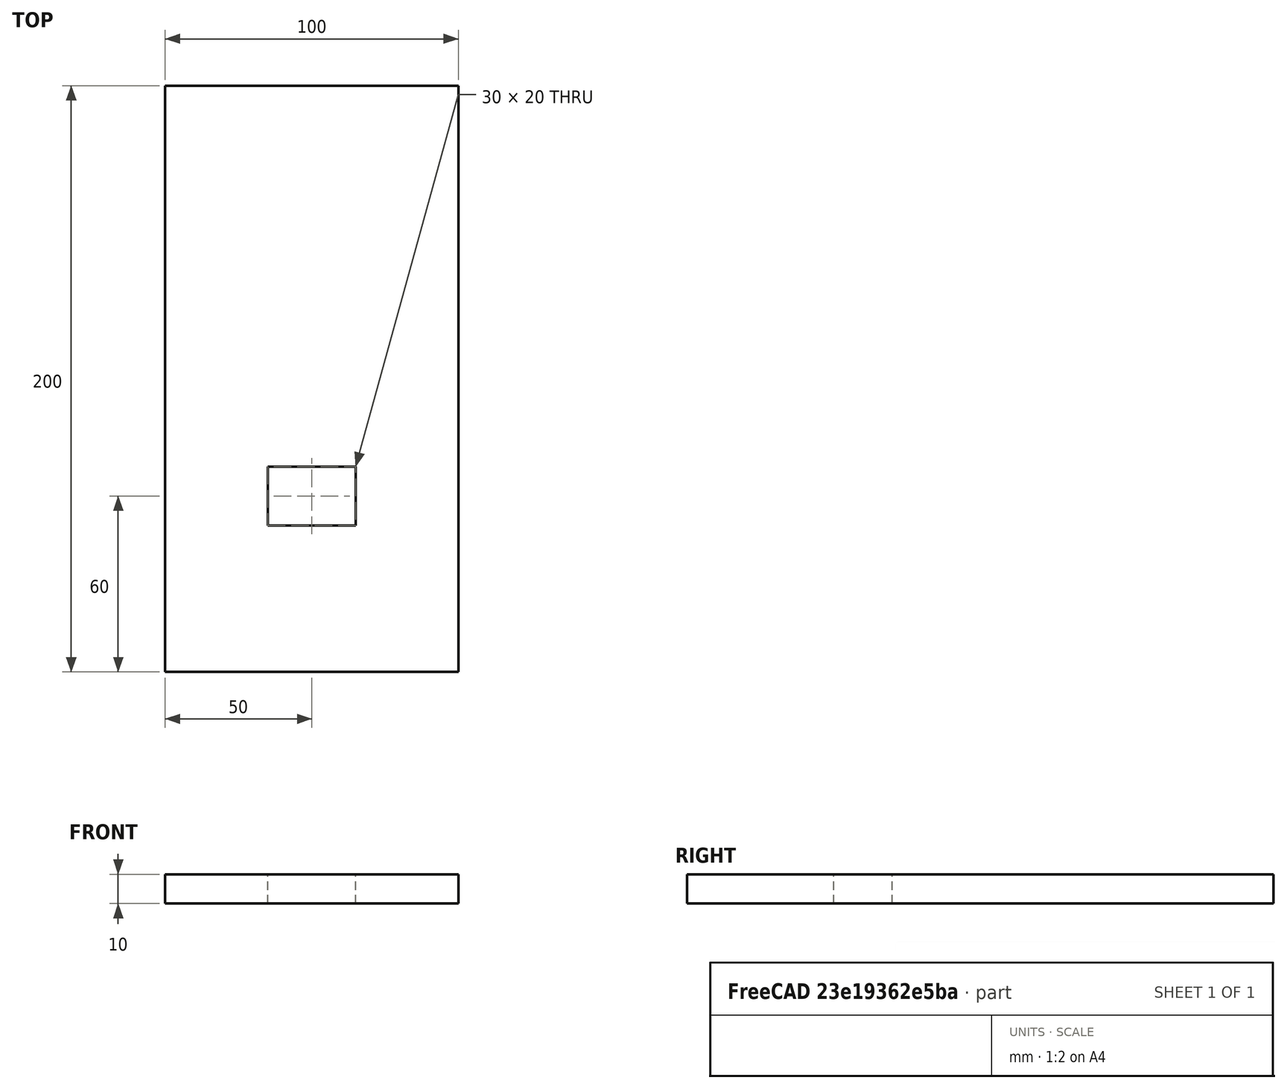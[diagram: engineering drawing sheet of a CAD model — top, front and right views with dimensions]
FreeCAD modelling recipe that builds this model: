
FCSTD DOCUMENT  (FreeCAD 0.16R6703 (Git))
Label: box_back
License: All rights reserved
LicenseURL: http://en.wikipedia.org/wiki/All_rights_reserved
objects: Sketcher::SketchObject×1, PartDesign::Pad×1
note: 3 computed .brp shape members not serialized (recipe doc carries the construction recipe); baked Part::Feature solids carry a one-line shape summary decoded from their .brp

FEATURE [Sketcher::SketchObject] Sketch
  expr: Constraints[21] = (100 - 30) / 2
  sketch-geometry (8):
    g0: LineSegment StartX=0 StartY=0 StartZ=0 EndX=100 EndY=0 EndZ=0
    g1: LineSegment StartX=100 StartY=0 StartZ=0 EndX=100 EndY=200 EndZ=0
    g2: LineSegment StartX=100 StartY=200 StartZ=0 EndX=0 EndY=200 EndZ=0
    g3: LineSegment StartX=0 StartY=200 StartZ=0 EndX=0 EndY=0 EndZ=0
    g4: LineSegment StartX=35 StartY=50 StartZ=0 EndX=65 EndY=50 EndZ=0
    g5: LineSegment StartX=65 StartY=50 StartZ=0 EndX=65 EndY=70 EndZ=0
    g6: LineSegment StartX=65 StartY=70 StartZ=0 EndX=35 EndY=70 EndZ=0
    g7: LineSegment StartX=35 StartY=70 StartZ=0 EndX=35 EndY=50 EndZ=0
  constraints (23):
    c: Coincident(g0,g1)
    c: Coincident(g1,g2)
    c: Coincident(g2,g3)
    c: Coincident(g3,g0)
    c: Horizontal(g0)
    c: Horizontal(g2)
    c: Vertical(g1)
    c: Vertical(g3)
    c: Coincident(g0,g-1)
    c: Distance(g3) = 200
    c: Distance(g0) = 100
    c: Coincident(g4,g5)
    c: Coincident(g5,g6)
    c: Coincident(g6,g7)
    c: Coincident(g7,g4)
    c: Horizontal(g4)
    c: Horizontal(g6)
    c: Vertical(g5)
    c: Vertical(g7)
    c: Distance(g6) = 30
    c: Distance(g5) = 20
    c: DistanceX(g4,g0) = 35
    c: DistanceY(g0,g4) = 50
FEATURE [PartDesign::Pad] Pad
  Length = 10
  Length2 = 100
  Sketch = -> Sketch
  Type = 0
